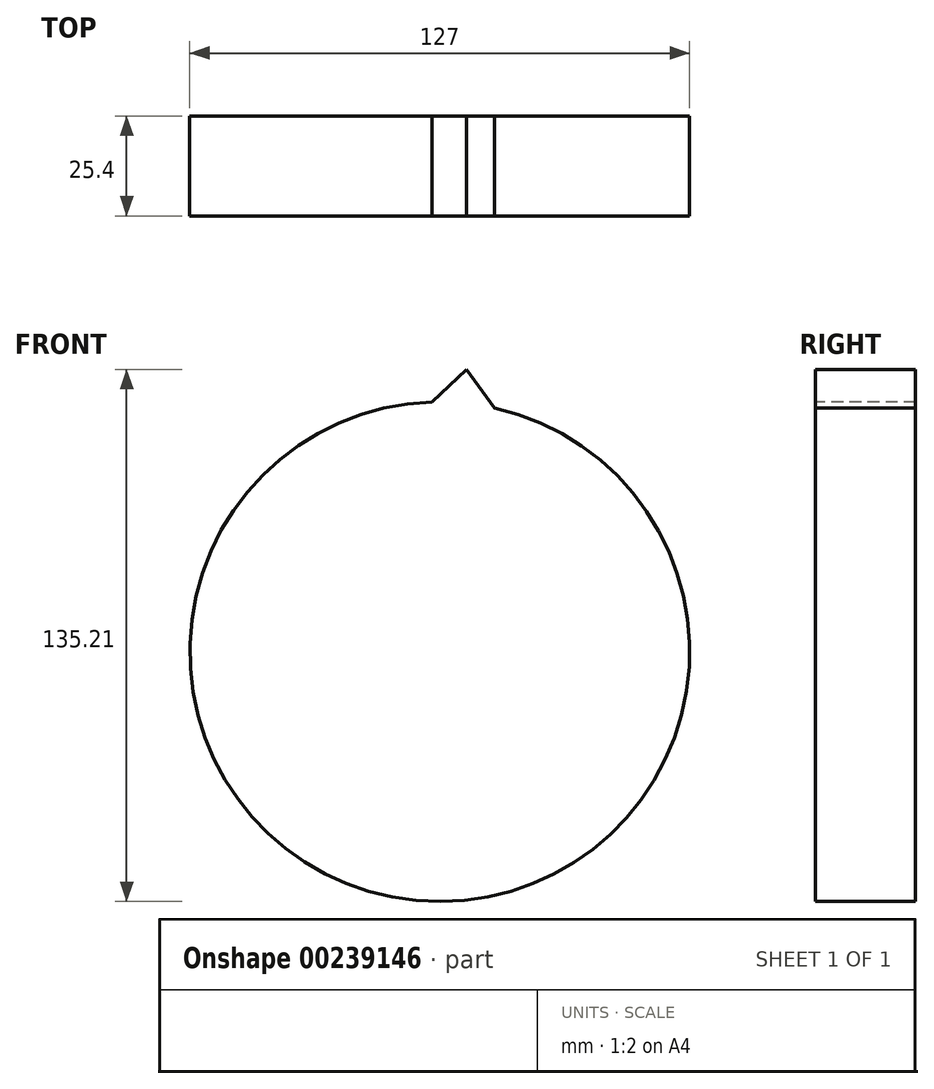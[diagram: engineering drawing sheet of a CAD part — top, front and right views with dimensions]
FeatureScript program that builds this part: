
annotation { "Feature Type Name" : "Feature", "Feature Type Description" : "" }
export const myFeature = defineFeature(function(context is Context, id is Id, definition is map)
    precondition{}
    {
        {
            var Q0;
            Q0=qCreatedBy(makeId("Front.planeOp"),FACE);
            var sketch = newSketch(context, id + "F0", { "sketchPlane" : qUnion([Q0])});
            skCircle(sketch, "E0", {"center": v(0, 0) * mm, "radius": 63.5 * mm});
            skSolve(sketch);
        }
        {
            var Q0;
            Q0 = qSketchRegion(id + "F0", true);
            extrude(context, id + "F1", {"entities" : qUnion([Q0]), "depth" : 25.4 * mm});
        }
        {
            var Q0;
            Q0=makeQuery(id+"F1.opExtrude","CAP_FACE",FACE,{"disambiguationData":[OSD([sQuery(id+"F0.wireOp",EDGE,"E0")])],"isStart":false});
            var sketch = newSketch(context, id + "F2", { "sketchPlane" : qUnion([Q0])});
            skLineSegment(sketch, "E1", {"start": v(-2.02, 63.47) * mm, "end": v(13.9, 61.96) * mm});
            skLineSegment(sketch, "E2", {"start": v(13.9, 61.96) * mm, "end": v(6.8, 71.71) * mm});
            skLineSegment(sketch, "E3", {"start": v(6.8, 71.71) * mm, "end": v(-2.02, 63.47) * mm});
            skSolve(sketch);
        }
        {
            var Q0;
            Q0 = qSketchRegion(id + "F2", true);
            extrude(context, id + "F3", {"entities" : qUnion([Q0]), "operationType" : NewBodyOperationType.ADD, "oppositeDirection" : true, "depth" : 25.4 * mm});
        }
    });
